# Revit family: 201_ROX _-180-3-RR
name_source: partatom
category: Air Terminals
units: mm (PartAtom-declared; Revit-internal decimal feet)

## family parameters
Always vertical = Yes
Cut with Voids When Loaded = No
Part Type = Normal
Room Calculation Point = Yes
Round Connector Dimension = Use Diameter
Shared = No
Work Plane-Based = No

## types (6) — shared parameters
CL_Location_5000 = 5000 mm  [stored 16.4042 ft]
Description = Supply air duct, length 4500mm
L = 4510 mm  [stored 14.7966 ft]
LL = 2255 mm  [stored 7.39829 ft]
L_ARR = 400 mm  [stored 1.31234 ft]
Manufacturer = Climecon
QmdConnectorList = 201;D
URL = www.climecon.fi
W_ARR = 400 mm  [stored 1.31234 ft]
XRefLineVPlnId = 7453
YRefLineVPlnId = 7456
magiPartTypeId = 201
magiProductFamilyId = ROX *-180-3-RR
zero-valued in all types: CLBTZ, H_ARR, MC_Default_elevation

## per-type parameters (varying)
| type | D | R |
| ROX 160-180-3-RR | 160 mm | 80 mm  [stored 0.262467 ft] |
| ROX 500-180-3-RR | 500 mm | 250 mm  [stored 0.82021 ft] |
| ROX 400-180-3-RR | 400 mm | 200 mm  [stored 0.656168 ft] |
| ROX 315-180-3-RR | 315 mm | 158 mm |
| ROX 250-180-3-RR | 250 mm | 125 mm  [stored 0.410105 ft] |
| ROX 200-180-3-RR | 200 mm | 100 mm  [stored 0.328084 ft] |

note: column(s) folded — value = type name in every type: magiProductCode, magiProductId

note: [stored X ft] marks values corroborated as IEEE doubles in the binary element streams (Revit-internal decimal feet)

## geometry (parser evidence)
native form markers: Sweep x2
no freeform markers — native parametric forms only
